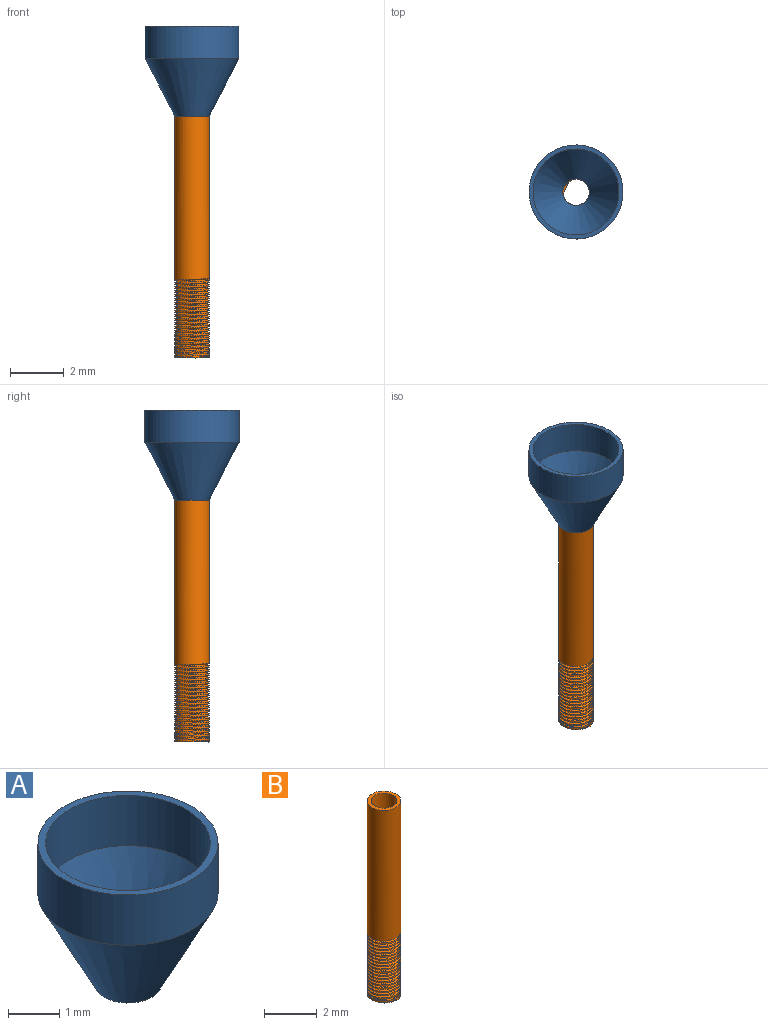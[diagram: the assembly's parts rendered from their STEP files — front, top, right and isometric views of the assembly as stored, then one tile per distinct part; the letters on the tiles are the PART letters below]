
ASSEMBLY  parts=2 mates=1
PART A: 6 faces, bbox 3.5x3.5x3.4 mm
  f0: plane 3.5x3.5mm, normal (0,0,1), area 1.6mm2, adj f1,f5
  f1: cylinder r=1.75mm len=3.5mm, axis (0,0,-1), area 13.1mm2, adj f0,f2
  f2: cone r=1.75mm half-angle=27.2deg, axis (0,0,1), area 18.2mm2, adj f1,f3
  f3: plane 1.29x1.29mm, normal (0,0,-1), area 0.5mm2, adj f2,f4
  f4: cone r=1.6mm half-angle=27.2deg, axis (0,0,1), area 15.9mm2, adj f3,f5
  f5: cylinder r=1.6mm len=3.2mm, axis (0,0,-1), area 12mm2, adj f0,f4
PART B: 27 faces, bbox 1.3x1.5x9.1 mm
  f0: cylinder r=0.49mm len=9mm, axis (0,0,-1), area 27.9mm2, adj f22,f23
  f1: cylinder r=0.64mm len=6.19mm, axis (0,0,-1), area 24.7mm2, adj f2,f22,f24,f26
  f2: cylinder r=0.64mm len=1.29mm, axis (0,0,-1), area 0.3mm2, adj f1,f3,f24,f25
  f3: cylinder r=0.64mm len=1.29mm, axis (0,0,-1), area 0.3mm2, adj f2,f4,f24,f25
  f4: cylinder r=0.64mm len=1.29mm, axis (0,0,-1), area 0.3mm2, adj f3,f5,f24,f25
  f5: cylinder r=0.64mm len=1.29mm, axis (0,0,-1), area 0.3mm2, adj f4,f6,f24,f25
  f6: cylinder r=0.64mm len=1.29mm, axis (0,0,-1), area 0.3mm2, adj f5,f7,f24,f25
  f7: cylinder r=0.64mm len=1.29mm, axis (0,0,-1), area 0.3mm2, adj f6,f8,f24,f25
  f8: cylinder r=0.64mm len=1.29mm, axis (0,0,-1), area 0.3mm2, adj f7,f9,f24,f25
  f9: cylinder r=0.64mm len=1.29mm, axis (0,0,-1), area 0.3mm2, adj f8,f10,f24,f25
  f10: cylinder r=0.64mm len=1.29mm, axis (0,0,-1), area 0.3mm2, adj f9,f11,f24,f25
  f11: cylinder r=0.64mm len=1.29mm, axis (0,0,-1), area 0.3mm2, adj f10,f12,f24,f25
  f12: cylinder r=0.64mm len=1.29mm, axis (0,0,-1), area 0.3mm2, adj f11,f13,f24,f25
  f13: cylinder r=0.64mm len=1.29mm, axis (0,0,-1), area 0.3mm2, adj f12,f14,f24,f25
  f14: cylinder r=0.64mm len=1.29mm, axis (0,0,-1), area 0.3mm2, adj f13,f15,f24,f25
  f15: cylinder r=0.64mm len=1.29mm, axis (0,0,-1), area 0.3mm2, adj f14,f16,f24,f25
  f16: cylinder r=0.64mm len=1.29mm, axis (0,0,-1), area 0.3mm2, adj f15,f17,f24,f25
  f17: cylinder r=0.64mm len=1.29mm, axis (0,0,-1), area 0.3mm2, adj f16,f18,f24,f25
  f18: cylinder r=0.64mm len=1.29mm, axis (0,0,-1), area 0.3mm2, adj f17,f19,f24,f25
  f19: cylinder r=0.64mm len=1.29mm, axis (0,0,-1), area 0.3mm2, adj f18,f20,f24,f25
  f20: cylinder r=0.64mm len=1.29mm, axis (0,0,-1), area 0.3mm2, adj f19,f21,f23,f24,f25
  f21: cylinder r=0.64mm len=0.61mm, axis (0,0,-1), area 0mm2, adj f20,f23,f25
  f22: plane 1.29x1.29mm, normal (0,0,1), area 0.5mm2, adj f0,f1
  f23: plane 1.31x1.26mm, normal (0,0,-1), area 0.5mm2, adj f0,f20,f21,f24,f25
  f24: bspline ~3.02x1.48mm, area 6mm2, adj f1,f2,f3,f4,f5,f6,f7,f8
  f25: bspline ~2.96x1.29mm, area 5.9mm2, adj f2,f3,f4,f5,f6,f7,f8,f9
  f26: plane 0.08x0.07mm, normal (0,-1,0), area 0mm2, adj f1,f24,f25
PLACE A t=(-1.59,2.82,-12.81)mm
PLACE B t=(-1.59,2.82,-21.81)mm
MATE fastened B.f0 <-> A.f1  axis (0,0,1) through (-1.59,2.82,-12.81)mm
